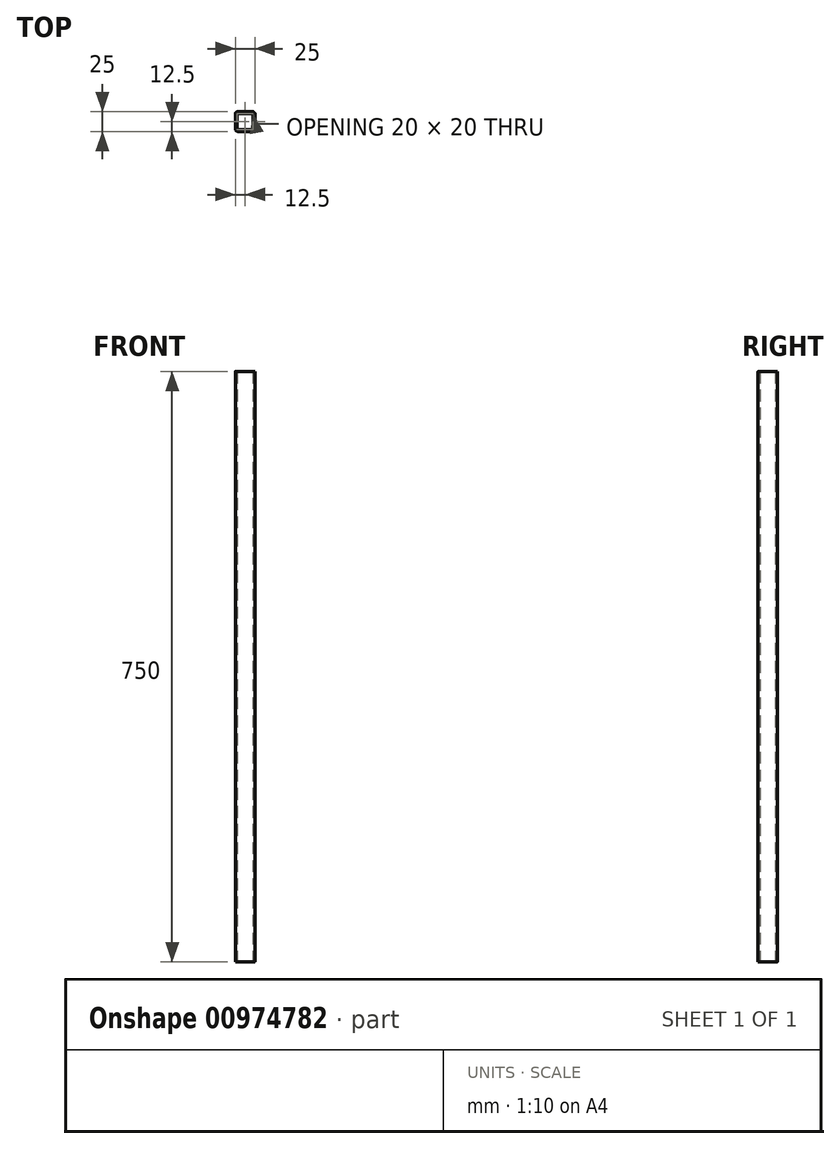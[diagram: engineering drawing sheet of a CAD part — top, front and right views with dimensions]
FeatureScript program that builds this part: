
annotation { "Feature Type Name" : "Feature", "Feature Type Description" : "" }
export const myFeature = defineFeature(function(context is Context, id is Id, definition is map)
    precondition{}
    {
        {
            var Q0;
            Q0=qCreatedBy(makeId("Top.planeOp"),FACE);
            var sketch = newSketch(context, id + "F0", { "sketchPlane" : qUnion([Q0])});
            skLineSegment(sketch, "E0.bottom", {"start": v(12.5, 12.5) * mm, "end": v(-12.5, 12.5) * mm});
            skLineSegment(sketch, "E0.top", {"start": v(12.5, -12.5) * mm, "end": v(-12.5, -12.5) * mm});
            skLineSegment(sketch, "E0.left", {"start": v(12.5, 12.5) * mm, "end": v(12.5, -12.5) * mm});
            skLineSegment(sketch, "E0.right", {"start": v(-12.5, 12.5) * mm, "end": v(-12.5, -12.5) * mm});
            skPoint(sketch, "E0.middle", {"position": v(0, 0) * mm});
            skLineSegment(sketch, "E1.bottom", {"start": v(10, 10) * mm, "end": v(-10, 10) * mm});
            skLineSegment(sketch, "E1.top", {"start": v(10, -10) * mm, "end": v(-10, -10) * mm});
            skLineSegment(sketch, "E1.left", {"start": v(10, 10) * mm, "end": v(10, -10) * mm});
            skLineSegment(sketch, "E1.right", {"start": v(-10, 10) * mm, "end": v(-10, -10) * mm});
            skSolve(sketch);
        }
        {
            var Q0;
            Q0=qSketchRegion(id+"F0",true);
            extrude(context, id + "F1", {"entities" : qUnion([Q0]), "depth" : 750 * mm, "offsetDistance" : 25 * mm});
        }
        {
            var Q0;
            Q0=makeQuery(id+"F1.opExtrude","SWEPT_EDGE",EDGE,{"disambiguationData":[OSD([sQuery(id+"F0.wireOp",EDGE,"E1.bottom"),sQuery(id+"F0.wireOp",EDGE,"E1.right")])]});
            var Q1;
            Q1=makeQuery(id+"F1.opExtrude","SWEPT_EDGE",EDGE,{"disambiguationData":[OSD([sQuery(id+"F0.wireOp",EDGE,"E1.bottom"),sQuery(id+"F0.wireOp",EDGE,"E1.left")])]});
            var Q2;
            Q2=makeQuery(id+"F1.opExtrude","SWEPT_EDGE",EDGE,{"disambiguationData":[OSD([sQuery(id+"F0.wireOp",EDGE,"E1.top"),sQuery(id+"F0.wireOp",EDGE,"E1.left")])]});
            var Q3;
            Q3=makeQuery(id+"F1.opExtrude","SWEPT_EDGE",EDGE,{"disambiguationData":[OSD([sQuery(id+"F0.wireOp",EDGE,"E1.top"),sQuery(id+"F0.wireOp",EDGE,"E1.right")])]});
            fillet(context, id + "F2", {"entities" : qUnion([Q0, Q1, Q2, Q3]), "radius" : 0.5 * mm, "tangentPropagation" : true, "allowEdgeOverflow" : false});
        }
        {
            var Q0;
            Q0=makeQuery(id+"F1.opExtrude","SWEPT_EDGE",EDGE,{"disambiguationData":[OSD([sQuery(id+"F0.wireOp",EDGE,"E0.bottom"),sQuery(id+"F0.wireOp",EDGE,"E0.left")])]});
            var Q1;
            Q1=makeQuery(id+"F1.opExtrude","SWEPT_EDGE",EDGE,{"disambiguationData":[OSD([sQuery(id+"F0.wireOp",EDGE,"E0.bottom"),sQuery(id+"F0.wireOp",EDGE,"E0.right")])]});
            var Q2;
            Q2=makeQuery(id+"F1.opExtrude","SWEPT_EDGE",EDGE,{"disambiguationData":[OSD([sQuery(id+"F0.wireOp",EDGE,"E0.top"),sQuery(id+"F0.wireOp",EDGE,"E0.left")])]});
            var Q3;
            Q3=makeQuery(id+"F1.opExtrude","SWEPT_EDGE",EDGE,{"disambiguationData":[OSD([sQuery(id+"F0.wireOp",EDGE,"E0.top"),sQuery(id+"F0.wireOp",EDGE,"E0.right")])]});
            fillet(context, id + "F3", {"entities" : qUnion([Q0, Q1, Q2, Q3]), "radius" : 3 * mm, "tangentPropagation" : true, "allowEdgeOverflow" : false});
        }
    });
